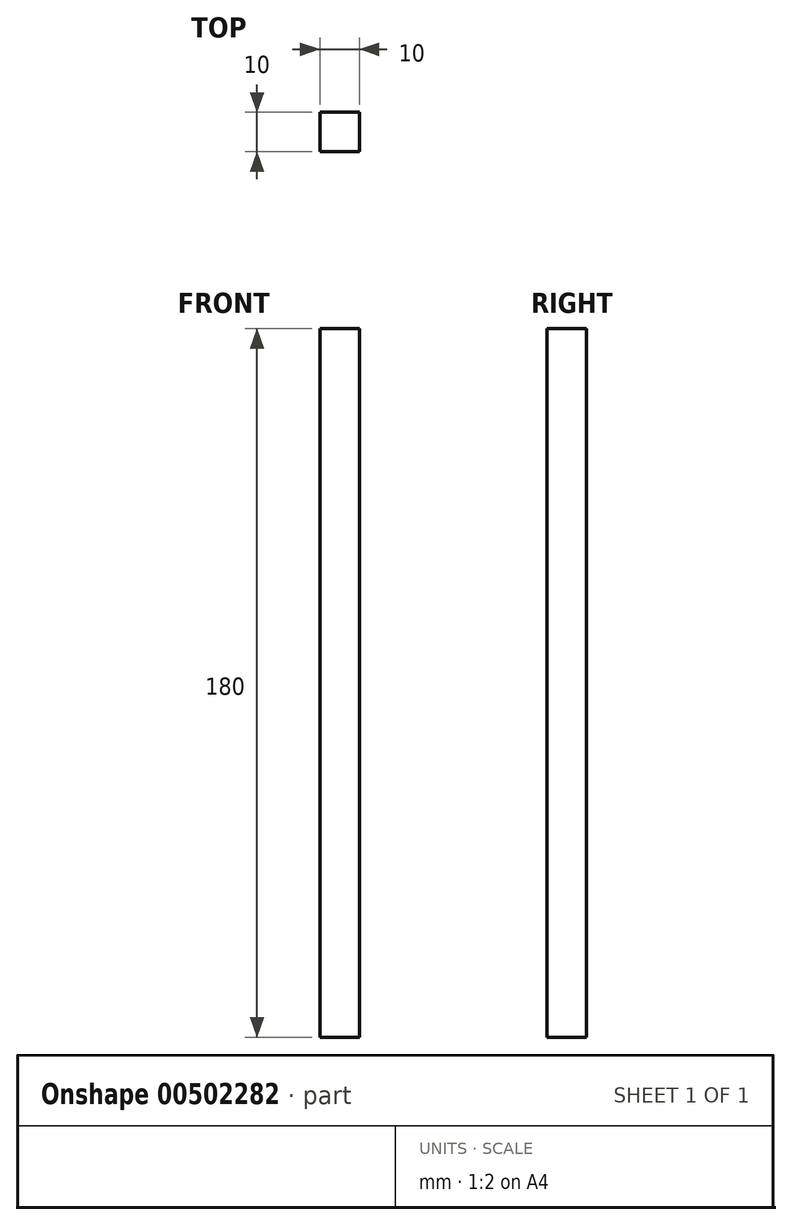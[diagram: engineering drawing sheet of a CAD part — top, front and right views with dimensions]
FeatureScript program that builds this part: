
annotation { "Feature Type Name" : "Feature", "Feature Type Description" : "" }
export const myFeature = defineFeature(function(context is Context, id is Id, definition is map)
    precondition{}
    {
        {
            var Q0;
            Q0=qCreatedBy(makeId("Top.planeOp"),FACE);
            var sketch = newSketch(context, id + "F0", { "sketchPlane" : qUnion([Q0])});
            skLineSegment(sketch, "E0.bottom", {"start": v(-5.68, 10) * mm, "end": v(4.32, 10) * mm});
            skLineSegment(sketch, "E0.top", {"start": v(-5.68, 0) * mm, "end": v(4.32, 0) * mm});
            skLineSegment(sketch, "E0.left", {"start": v(-5.68, 10) * mm, "end": v(-5.68, 0) * mm});
            skLineSegment(sketch, "E0.right", {"start": v(4.32, 10) * mm, "end": v(4.32, 0) * mm});
            skSolve(sketch);
        }
        {
            var Q0;
            Q0 = qSketchRegion(id + "F0", true);
            extrude(context, id + "F1", {"entities" : qUnion([Q0]), "depth" : 180 * mm});
        }
    });
